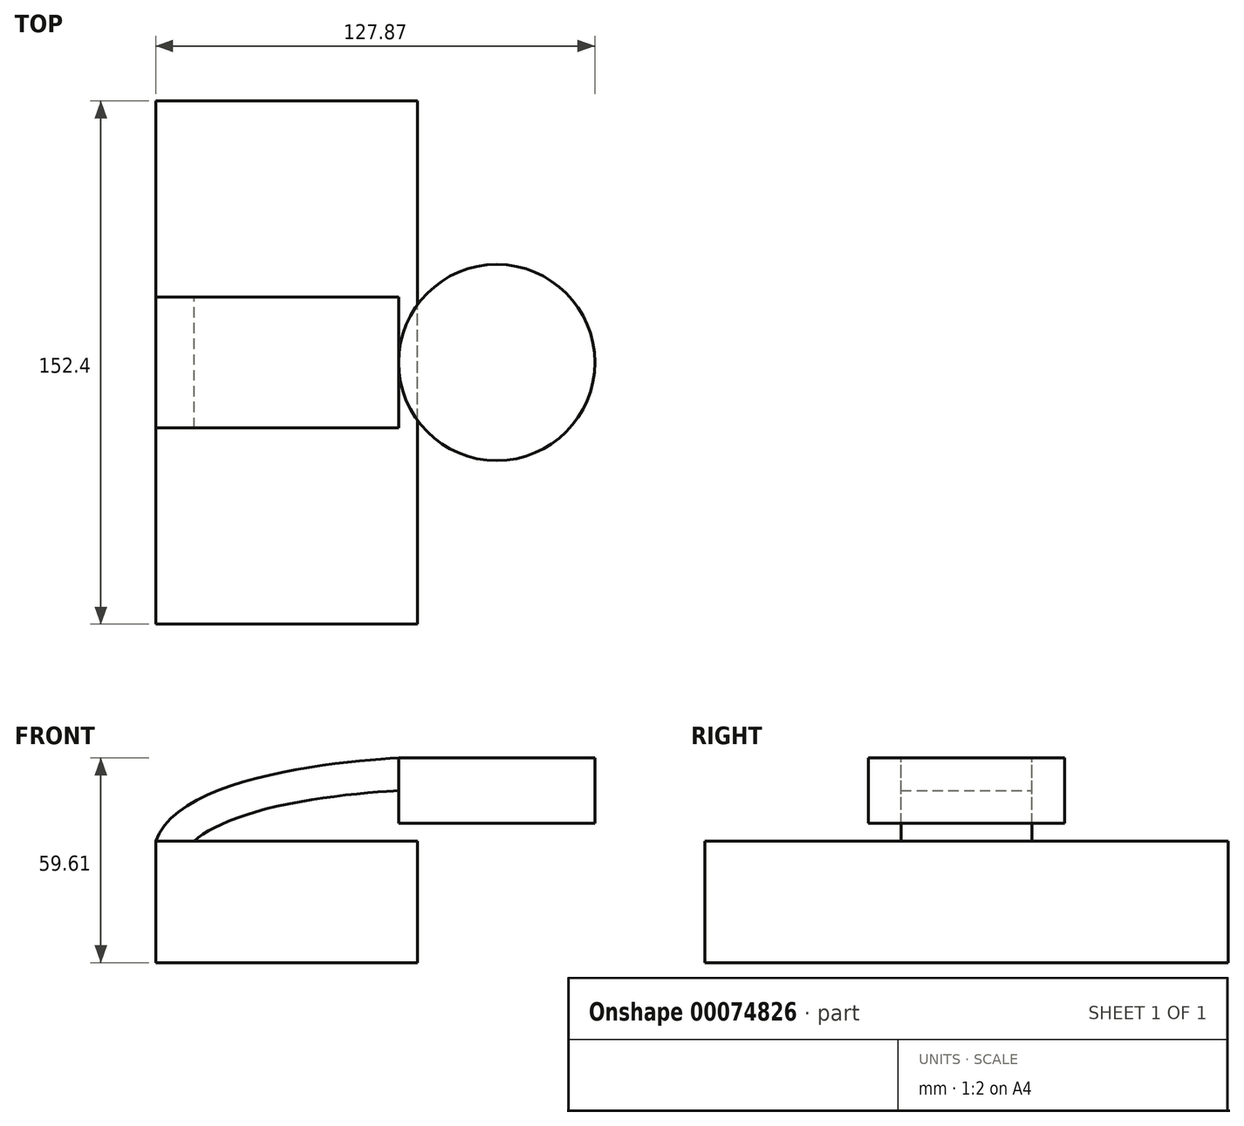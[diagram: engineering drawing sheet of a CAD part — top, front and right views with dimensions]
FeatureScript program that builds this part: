
annotation { "Feature Type Name" : "Feature", "Feature Type Description" : "" }
export const myFeature = defineFeature(function(context is Context, id is Id, definition is map)
    precondition{}
    {
        {
            var Q0;
            Q0=qCreatedBy(makeId("Front.planeOp"),FACE);
            var sketch = newSketch(context, id + "F0", { "sketchPlane" : qUnion([Q0])});
            skLineSegment(sketch, "E0.rect.bottom", {"start": v(38.1, -17.67) * mm, "end": v(-38.1, -17.67) * mm});
            skLineSegment(sketch, "E0.rect.top", {"start": v(38.1, 17.67) * mm, "end": v(-38.1, 17.67) * mm});
            skLineSegment(sketch, "E0.rect.left", {"start": v(38.1, -17.67) * mm, "end": v(38.1, 17.67) * mm});
            skLineSegment(sketch, "E0.rect.right", {"start": v(-38.1, -17.67) * mm, "end": v(-38.1, 17.67) * mm});
            skPoint(sketch, "E0.rect.middle", {"position": v(0, 0) * mm});
            skLineSegment(sketch, "E1.rect.bottom", {"start": v(61.2, 22.9) * mm, "end": v(32.62, 22.9) * mm});
            skLineSegment(sketch, "E1.rect.top", {"start": v(61.2, 41.94) * mm, "end": v(32.62, 41.94) * mm});
            skLineSegment(sketch, "E1.rect.left", {"start": v(61.2, 22.9) * mm, "end": v(61.2, 41.94) * mm});
            skLineSegment(sketch, "E1.rect.right", {"start": v(32.62, 22.9) * mm, "end": v(32.62, 41.94) * mm});
            skPoint(sketch, "E1.rect.middle", {"position": v(46.9, 32.42) * mm});
            skFitSpline(sketch, "E2", {"points": [v(-38.1, 17.67) * mm, v(32.62, 41.94) * mm], "startDerivative": vector(18.73, 56.23) * mm, "endDerivative": vector(52.54, 2.77) * mm});
            skFitSpline(sketch, "E3.0", {"points": [v(-29.06, 14.66) * mm, v(-29, 14.83) * mm, v(-28.86, 15.2) * mm, v(-28.51, 15.81) * mm, v(-28, 16.52) * mm, v(-27.04, 17.58) * mm, v(-25.3, 19.06) * mm, v(-22.38, 20.92) * mm, v(-18.72, 22.72) * mm, v(-13.05, 24.96) * mm, v(-4.83, 27.35) * mm, v(5.84, 29.52) * mm, v(16.39, 31.03) * mm, v(25.92, 31.99) * mm, v(31.03, 32.32) * mm, v(33.12, 32.43) * mm]});
            skSolve(sketch);
        }
        {
            var Q0;
            Q0=makeQuery(id+"F0.imprint","IMPRINT",FACE,{"disambiguationData":[TD([[makeQuery(id+"F0.imprint","IMPRINT",EDGE,{"derivedFrom":sQuery(id+"F0.wireOp",EDGE,"E0.rect.bottom")}),-1.0]])]});
            extrude(context, id + "F1", {"entities" : qUnion([Q0]), "endBound" : BoundingType.SYMMETRIC, "depth" : 152.4 * mm});
        }
        {
            var Q0;
            {var subQ1=sQuery(id+"F0.wireOp",EDGE,"E1.rect.bottom");Q0=makeQuery(id+"F0.imprint","IMPRINT",FACE,{"disambiguationData":[TD([[makeQuery(id+"F0.imprint","IMPRINT",EDGE,{"derivedFrom":subQ1}),-1.0]])]});}
            var Q1;
            Q1=sQuery(id+"F0.wireOp",EDGE,"E1.rect.left");
            revolve(context, id + "F2", {"entities" : qUnion([Q0]), "axis" : qUnion([Q1]), "revolveType" : RevolveType.FULL});
        }
        {
            var Q0;
            {var subQ0=sQuery(id+"F0.wireOp",EDGE,"E2");Q0=makeQuery(id+"F0.imprint","IMPRINT",FACE,{"disambiguationData":[TD([[makeQuery(id+"F0.imprint","IMPRINT",EDGE,{"derivedFrom":subQ0}),-1.0]])]});}
            extrude(context, id + "F3", {"entities" : qUnion([Q0]), "operationType" : NewBodyOperationType.ADD, "endBound" : BoundingType.SYMMETRIC, "depth" : 38.1 * mm});
        }
    });
